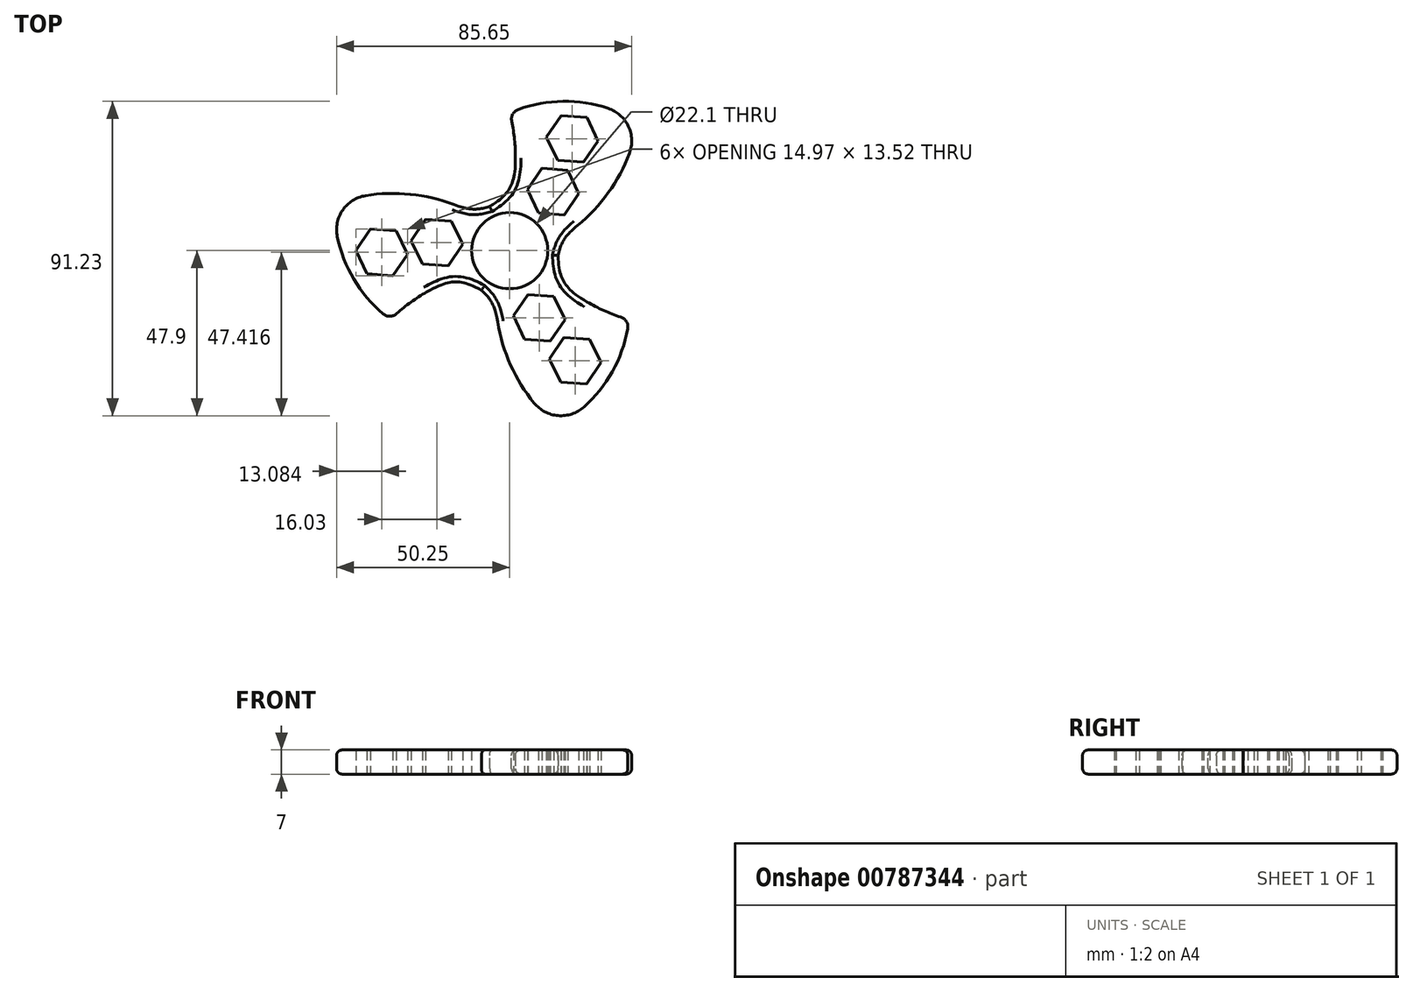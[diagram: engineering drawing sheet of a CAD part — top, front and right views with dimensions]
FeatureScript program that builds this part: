
annotation { "Feature Type Name" : "Feature", "Feature Type Description" : "" }
export const myFeature = defineFeature(function(context is Context, id is Id, definition is map)
    precondition{}
    {
        {
            var Q0;
            Q0=qCreatedBy(makeId("Top.planeOp"),FACE);
            var sketch = newSketch(context, id + "F0", { "sketchPlane" : qUnion([Q0])});
            skCircle(sketch, "E0", {"center": v(0, 0) * mm, "radius": 14 * mm});
            skArc(sketch, "E1", {"start": v(0, 14) * mm, "mid": v(1.66, 27) * mm, "end": v(0, 40) * mm});
            skPoint(sketch, "E2", {"position": v(0, 40) * mm});
            skLineSegment(sketch, "E3", {"start": v(0, 0) * mm, "end": v(37.22, 37.22) * mm, "construction": true});
            skPoint(sketch, "E4", {"position": v(37.22, 37.22) * mm});
            skArc(sketch, "E5.trimOffspring", {"start": v(37.22, 37.22) * mm, "mid": v(18.96, 43.22) * mm, "end": v(0, 40) * mm});
            skArc(sketch, "E6.trimOffspring", {"start": v(13.66, 3.08) * mm, "mid": v(29.15, 17.6) * mm, "end": v(37.22, 37.22) * mm});
            skCircle(sketch, "E7", {"center": v(0, 0) * mm, "radius": 11.05 * mm});
            skCircle(sketch, "E8.cCircle", {"center": v(18.16, 32.43) * mm, "radius": 6.5 * mm, "construction": true});
            skLineSegment(sketch, "E8.0", {"start": v(25.65, 31.87) * mm, "end": v(21.42, 25.67) * mm});
            skLineSegment(sketch, "E8.1", {"start": v(21.42, 25.67) * mm, "end": v(13.94, 26.23) * mm});
            skLineSegment(sketch, "E8.2", {"start": v(13.94, 26.23) * mm, "end": v(10.68, 32.99) * mm});
            skLineSegment(sketch, "E8.3", {"start": v(10.68, 32.99) * mm, "end": v(14.9, 39.19) * mm});
            skLineSegment(sketch, "E8.4", {"start": v(14.9, 39.19) * mm, "end": v(22.39, 38.63) * mm});
            skLineSegment(sketch, "E8.5", {"start": v(22.39, 38.63) * mm, "end": v(25.65, 31.87) * mm});
            skPoint(sketch, "E8.0.midPoint", {"position": v(23.54, 28.77) * mm});
            skLineSegment(sketch, "E9", {"start": v(18.65, 38.91) * mm, "end": v(18.16, 32.43) * mm, "construction": true});
            skLineSegment(sketch, "E10", {"start": v(0, 14) * mm, "end": v(13.66, 3.08) * mm, "construction": true});
            skLineSegment(sketch, "E11", {"start": v(6.83, 8.54) * mm, "end": v(20.57, 25.73) * mm, "construction": true});
            skLineSegment(sketch, "E12", {"start": v(37.22, 37.22) * mm, "end": v(0, 40) * mm, "construction": true});
            skCircle(sketch, "E13.cCircle", {"center": v(12.6, 17.14) * mm, "radius": 6.5 * mm, "construction": true});
            skLineSegment(sketch, "E13.0", {"start": v(9.33, 23.9) * mm, "end": v(16.82, 23.34) * mm});
            skLineSegment(sketch, "E13.1", {"start": v(16.82, 23.34) * mm, "end": v(20.08, 16.58) * mm});
            skLineSegment(sketch, "E13.2", {"start": v(20.08, 16.58) * mm, "end": v(15.85, 10.38) * mm});
            skLineSegment(sketch, "E13.3", {"start": v(15.85, 10.38) * mm, "end": v(8.36, 10.93) * mm});
            skLineSegment(sketch, "E13.4", {"start": v(8.36, 10.93) * mm, "end": v(5.1, 17.7) * mm});
            skLineSegment(sketch, "E13.5", {"start": v(5.1, 17.7) * mm, "end": v(9.33, 23.9) * mm});
            skPoint(sketch, "E13.0.midPoint", {"position": v(13.07, 23.62) * mm});
            skPoint(sketch, "E14.1.18", {"position": v(-1.49, 0.86) * mm});
            skPoint(sketch, "E14.1.24", {"position": v(-1.49, 0.86) * mm});
            skPoint(sketch, "E14.2.18", {"position": v(-1.49, -0.86) * mm});
            skPoint(sketch, "E14.2.24", {"position": v(-1.49, -0.86) * mm});
            skPoint(sketch, "E14.center", {"position": v(-1, 0) * mm});
            skPoint(sketch, "E15", {"position": v(13.7, 17.14) * mm});
            skCircle(sketch, "E16.1.0", {"center": v(-21.14, 2.34) * mm, "radius": 6.5 * mm, "construction": true});
            skLineSegment(sketch, "E16.1.1", {"start": v(-33.9, -7.24) * mm, "end": v(-41.4, -6.69) * mm});
            skPoint(sketch, "E16.1.2", {"position": v(1.49, -0.86) * mm});
            skLineSegment(sketch, "E16.1.3", {"start": v(-10.81, 1.64) * mm, "end": v(-32.57, 4.95) * mm, "construction": true});
            skArc(sketch, "E16.1.4", {"start": v(-50.85, 13.62) * mm, "mid": v(-46.9, -5.2) * mm, "end": v(-34.64, -20) * mm});
            skLineSegment(sketch, "E16.1.5", {"start": v(-24.4, 9.1) * mm, "end": v(-16.91, 8.54) * mm});
            skLineSegment(sketch, "E16.1.6", {"start": v(-50.85, 13.62) * mm, "end": v(-34.64, -20) * mm, "construction": true});
            skLineSegment(sketch, "E16.1.8", {"start": v(-28.62, 2.9) * mm, "end": v(-24.4, 9.1) * mm});
            skArc(sketch, "E16.1.9", {"start": v(-12.12, -7) * mm, "mid": v(-24.21, -12.06) * mm, "end": v(-34.64, -20) * mm});
            skLineSegment(sketch, "E16.1.10", {"start": v(-44.65, 0.07) * mm, "end": v(-40.42, 6.28) * mm});
            skPoint(sketch, "E16.1.11", {"position": v(-21.69, 3.3) * mm});
            skLineSegment(sketch, "E16.1.12", {"start": v(-17.88, -4.43) * mm, "end": v(-25.36, -3.87) * mm});
            skCircle(sketch, "E16.1.13", {"center": v(-37.17, -0.48) * mm, "radius": 6.5 * mm, "construction": true});
            skArc(sketch, "E16.1.14", {"start": v(-9.5, 10.28) * mm, "mid": v(-29.81, 16.45) * mm, "end": v(-50.85, 13.62) * mm});
            skPoint(sketch, "E16.1.15", {"position": v(-50.85, 13.62) * mm});
            skLineSegment(sketch, "E16.1.16", {"start": v(-29.68, -1.04) * mm, "end": v(-33.9, -7.24) * mm});
            skPoint(sketch, "E16.1.17", {"position": v(-36.68, 6) * mm});
            skLineSegment(sketch, "E16.1.18", {"start": v(-16.91, 8.54) * mm, "end": v(-13.65, 1.78) * mm});
            skLineSegment(sketch, "E16.1.19", {"start": v(-12.12, -7) * mm, "end": v(-9.5, 10.28) * mm, "construction": true});
            skLineSegment(sketch, "E16.1.20", {"start": v(-43.02, -3.3) * mm, "end": v(-37.17, -0.48) * mm, "construction": true});
            skPoint(sketch, "E16.1.21", {"position": v(-34.64, -20) * mm});
            skPoint(sketch, "E16.1.22", {"position": v(0.5, -0.86) * mm});
            skPoint(sketch, "E16.1.23", {"position": v(-27, -0.49) * mm});
            skPoint(sketch, "E16.1.24", {"position": v(1.49, -0.86) * mm});
            skLineSegment(sketch, "E16.1.25", {"start": v(-40.42, 6.28) * mm, "end": v(-32.94, 5.72) * mm});
            skLineSegment(sketch, "E16.1.26", {"start": v(-32.94, 5.72) * mm, "end": v(-29.68, -1.04) * mm});
            skLineSegment(sketch, "E16.1.27", {"start": v(-41.4, -6.69) * mm, "end": v(-44.65, 0.07) * mm});
            skLineSegment(sketch, "E16.1.29", {"start": v(-25.36, -3.87) * mm, "end": v(-28.62, 2.9) * mm});
            skLineSegment(sketch, "E16.1.30", {"start": v(-13.65, 1.78) * mm, "end": v(-17.88, -4.43) * mm});
            skCircle(sketch, "E16.2.0", {"center": v(8.55, -19.47) * mm, "radius": 6.5 * mm, "construction": true});
            skLineSegment(sketch, "E16.2.1", {"start": v(23.23, -25.74) * mm, "end": v(26.49, -32.5) * mm});
            skPoint(sketch, "E16.2.2", {"position": v(0, 1.72) * mm});
            skLineSegment(sketch, "E16.2.3", {"start": v(3.98, -10.18) * mm, "end": v(12, -30.68) * mm, "construction": true});
            skArc(sketch, "E16.2.4", {"start": v(13.62, -50.85) * mm, "mid": v(27.95, -38.03) * mm, "end": v(34.64, -20) * mm});
            skLineSegment(sketch, "E16.2.5", {"start": v(4.32, -25.68) * mm, "end": v(1.06, -18.91) * mm});
            skLineSegment(sketch, "E16.2.6", {"start": v(13.62, -50.85) * mm, "end": v(34.64, -20) * mm, "construction": true});
            skLineSegment(sketch, "E16.2.8", {"start": v(11.8, -26.23) * mm, "end": v(4.32, -25.68) * mm});
            skArc(sketch, "E16.2.9", {"start": v(12.12, -7) * mm, "mid": v(22.55, -14.94) * mm, "end": v(34.64, -20) * mm});
            skLineSegment(sketch, "E16.2.10", {"start": v(22.26, -38.7) * mm, "end": v(14.78, -38.15) * mm});
            skPoint(sketch, "E16.2.11", {"position": v(8, -20.43) * mm});
            skLineSegment(sketch, "E16.2.12", {"start": v(12.77, -13.27) * mm, "end": v(16.03, -20.03) * mm});
            skCircle(sketch, "E16.2.13", {"center": v(19, -31.94) * mm, "radius": 6.5 * mm, "construction": true});
            skArc(sketch, "E16.2.14", {"start": v(-4.16, -13.37) * mm, "mid": v(0.66, -34.04) * mm, "end": v(13.62, -50.85) * mm});
            skPoint(sketch, "E16.2.15", {"position": v(13.62, -50.85) * mm});
            skLineSegment(sketch, "E16.2.16", {"start": v(15.74, -25.18) * mm, "end": v(23.23, -25.74) * mm});
            skPoint(sketch, "E16.2.17", {"position": v(13.15, -34.77) * mm});
            skLineSegment(sketch, "E16.2.18", {"start": v(1.06, -18.91) * mm, "end": v(5.29, -12.71) * mm});
            skLineSegment(sketch, "E16.2.19", {"start": v(12.12, -7) * mm, "end": v(-4.16, -13.37) * mm, "construction": true});
            skLineSegment(sketch, "E16.2.20", {"start": v(24.37, -35.6) * mm, "end": v(19, -31.94) * mm, "construction": true});
            skPoint(sketch, "E16.2.21", {"position": v(34.64, -20) * mm});
            skPoint(sketch, "E16.2.22", {"position": v(0.5, 0.86) * mm});
            skPoint(sketch, "E16.2.23", {"position": v(13.92, -23.13) * mm});
            skPoint(sketch, "E16.2.24", {"position": v(0, 1.72) * mm});
            skLineSegment(sketch, "E16.2.25", {"start": v(14.78, -38.15) * mm, "end": v(11.52, -31.39) * mm});
            skLineSegment(sketch, "E16.2.26", {"start": v(11.52, -31.39) * mm, "end": v(15.74, -25.18) * mm});
            skLineSegment(sketch, "E16.2.27", {"start": v(26.49, -32.5) * mm, "end": v(22.26, -38.7) * mm});
            skLineSegment(sketch, "E16.2.29", {"start": v(16.03, -20.03) * mm, "end": v(11.8, -26.23) * mm});
            skLineSegment(sketch, "E16.2.30", {"start": v(5.29, -12.71) * mm, "end": v(12.77, -13.27) * mm});
            skSolve(sketch);
        }
        {
            var Q0;
            Q0 = qSketchRegion(id + "F0", true);
            extrude(context, id + "F1", {"entities" : qUnion([Q0]), "depth" : 7 * mm, "offsetDistance" : 25 * mm});
        }
        {
            var Q0;
            Q0=makeQuery(id+"F1.opExtrude","SWEPT_EDGE",EDGE,{"disambiguationData":[OSD([sQuery(id+"F0.wireOp",EDGE,"E16.1.4"),sQuery(id+"F0.wireOp",EDGE,"E16.1.14")])]});
            var Q1;
            Q1=makeQuery(id+"F1.opExtrude","SWEPT_EDGE",EDGE,{"disambiguationData":[OSD([sQuery(id+"F0.wireOp",EDGE,"E5.trimOffspring"),sQuery(id+"F0.wireOp",EDGE,"E6.trimOffspring")])]});
            var Q2;
            Q2=makeQuery(id+"F1.opExtrude","SWEPT_EDGE",EDGE,{"disambiguationData":[OSD([sQuery(id+"F0.wireOp",EDGE,"E16.2.4"),sQuery(id+"F0.wireOp",EDGE,"E16.2.14")])]});
            fillet(context, id + "F2", {"entities" : qUnion([Q0, Q1, Q2]), "radius" : 10 * mm, "tangentPropagation" : true, "allowEdgeOverflow" : false});
        }
        {
            var Q0;
            Q0=makeQuery(id+"F1.opExtrude","SWEPT_EDGE",EDGE,{"disambiguationData":[OSD([sQuery(id+"F0.wireOp",EDGE,"E1"),sQuery(id+"F0.wireOp",EDGE,"E5.trimOffspring")])]});
            var Q1;
            Q1=makeQuery(id+"F1.opExtrude","SWEPT_EDGE",EDGE,{"disambiguationData":[OSD([sQuery(id+"F0.wireOp",EDGE,"E16.1.4"),sQuery(id+"F0.wireOp",EDGE,"E16.1.9")])]});
            var Q2;
            Q2=makeQuery(id+"F1.opExtrude","SWEPT_EDGE",EDGE,{"disambiguationData":[OSD([sQuery(id+"F0.wireOp",EDGE,"E16.2.4"),sQuery(id+"F0.wireOp",EDGE,"E16.2.9")])]});
            fillet(context, id + "F3", {"entities" : qUnion([Q0, Q1, Q2]), "radius" : 3 * mm, "tangentPropagation" : true, "allowEdgeOverflow" : false});
        }
        {
            var Q0;
            Q0=makeQuery(id+"F1.opExtrude","SWEPT_EDGE",EDGE,{"disambiguationData":[OSD([sQuery(id+"F0.wireOp",EDGE,"E0"),sQuery(id+"F0.wireOp",EDGE,"544d86c7-8deb-4338-a2d6-1758b23e3787.2.16")])]});
            var Q1;
            Q1=makeQuery(id+"F1.opExtrude","SWEPT_EDGE",EDGE,{"disambiguationData":[OSD([sQuery(id+"F0.wireOp",EDGE,"E0"),sQuery(id+"F0.wireOp",EDGE,"E6.trimOffspring")])]});
            var Q2;
            Q2=makeQuery(id+"F1.opExtrude","SWEPT_EDGE",EDGE,{"disambiguationData":[OSD([sQuery(id+"F0.wireOp",EDGE,"E0"),sQuery(id+"F0.wireOp",EDGE,"E1")])]});
            var Q3;
            Q3=makeQuery(id+"F1.opExtrude","SWEPT_EDGE",EDGE,{"disambiguationData":[OSD([sQuery(id+"F0.wireOp",EDGE,"E0"),sQuery(id+"F0.wireOp",EDGE,"544d86c7-8deb-4338-a2d6-1758b23e3787.1.5")])]});
            var Q4;
            Q4=makeQuery(id+"F1.opExtrude","SWEPT_EDGE",EDGE,{"disambiguationData":[OSD([sQuery(id+"F0.wireOp",EDGE,"E0"),sQuery(id+"F0.wireOp",EDGE,"544d86c7-8deb-4338-a2d6-1758b23e3787.1.16")])]});
            var Q5;
            Q5=makeQuery(id+"F1.opExtrude","SWEPT_EDGE",EDGE,{"disambiguationData":[OSD([sQuery(id+"F0.wireOp",EDGE,"E0"),sQuery(id+"F0.wireOp",EDGE,"544d86c7-8deb-4338-a2d6-1758b23e3787.2.5")])]});
            fillet(context, id + "F4", {"entities" : qUnion([Q0, Q1, Q2, Q3, Q4, Q5]), "radius" : 17 * mm, "rho" : .6, "crossSection" : FilletCrossSection.CONIC, "allowEdgeOverflow" : false});
        }
        {
            var Q0;
            {var subQ0=sQuery(id+"F0.wireOp",EDGE,"E6.trimOffspring");var subQ1=sQuery(id+"F0.wireOp",EDGE,"E5.trimOffspring");Q0=makeQuery(id+"F2.opFillet","BLEND_EDGE",EDGE,{"blendedFrom":[makeQuery(id+"F1.opExtrude","SWEPT_EDGE",EDGE,{"disambiguationData":[OSD([subQ1,subQ0])]}),makeQuery(id+"F1.opExtrude","CAP_FACE",FACE,{"disambiguationData":[OSD([sQuery(id+"F0.wireOp",EDGE,"E0"),sQuery(id+"F0.wireOp",EDGE,"E1"),subQ1,subQ0,sQuery(id+"F0.wireOp",EDGE,"E7"),sQuery(id+"F0.wireOp",EDGE,"E8.0"),sQuery(id+"F0.wireOp",EDGE,"E8.1"),sQuery(id+"F0.wireOp",EDGE,"E8.2"),sQuery(id+"F0.wireOp",EDGE,"E8.3"),sQuery(id+"F0.wireOp",EDGE,"E8.4"),sQuery(id+"F0.wireOp",EDGE,"E8.5"),sQuery(id+"F0.wireOp",EDGE,"E13.0"),sQuery(id+"F0.wireOp",EDGE,"E13.1"),sQuery(id+"F0.wireOp",EDGE,"E13.2"),sQuery(id+"F0.wireOp",EDGE,"E13.3"),sQuery(id+"F0.wireOp",EDGE,"E13.4"),sQuery(id+"F0.wireOp",EDGE,"E13.5"),sQuery(id+"F0.wireOp",EDGE,"E16.1.1"),sQuery(id+"F0.wireOp",EDGE,"E16.1.4"),sQuery(id+"F0.wireOp",EDGE,"E16.1.5"),sQuery(id+"F0.wireOp",EDGE,"E16.1.8"),sQuery(id+"F0.wireOp",EDGE,"E16.1.9"),sQuery(id+"F0.wireOp",EDGE,"E16.1.10"),sQuery(id+"F0.wireOp",EDGE,"E16.1.12"),sQuery(id+"F0.wireOp",EDGE,"E16.1.14"),sQuery(id+"F0.wireOp",EDGE,"E16.1.16"),sQuery(id+"F0.wireOp",EDGE,"E16.1.18"),sQuery(id+"F0.wireOp",EDGE,"E16.1.25"),sQuery(id+"F0.wireOp",EDGE,"E16.1.26"),sQuery(id+"F0.wireOp",EDGE,"E16.1.27"),sQuery(id+"F0.wireOp",EDGE,"E16.1.29"),sQuery(id+"F0.wireOp",EDGE,"E16.1.30"),sQuery(id+"F0.wireOp",EDGE,"E16.2.1"),sQuery(id+"F0.wireOp",EDGE,"E16.2.4"),sQuery(id+"F0.wireOp",EDGE,"E16.2.5"),sQuery(id+"F0.wireOp",EDGE,"E16.2.8"),sQuery(id+"F0.wireOp",EDGE,"E16.2.9"),sQuery(id+"F0.wireOp",EDGE,"E16.2.10"),sQuery(id+"F0.wireOp",EDGE,"E16.2.12"),sQuery(id+"F0.wireOp",EDGE,"E16.2.14"),sQuery(id+"F0.wireOp",EDGE,"E16.2.16"),sQuery(id+"F0.wireOp",EDGE,"E16.2.18"),sQuery(id+"F0.wireOp",EDGE,"E16.2.25"),sQuery(id+"F0.wireOp",EDGE,"E16.2.26"),sQuery(id+"F0.wireOp",EDGE,"E16.2.27"),sQuery(id+"F0.wireOp",EDGE,"E16.2.29"),sQuery(id+"F0.wireOp",EDGE,"E16.2.30")])],"isStart":false})],"blendedInto":[makeQuery(id+"F1.opExtrude","CAP_FACE",FACE,{"disambiguationData":[OSD([sQuery(id+"F0.wireOp",EDGE,"E0"),sQuery(id+"F0.wireOp",EDGE,"E1"),subQ1,subQ0,sQuery(id+"F0.wireOp",EDGE,"E7"),sQuery(id+"F0.wireOp",EDGE,"E8.0"),sQuery(id+"F0.wireOp",EDGE,"E8.1"),sQuery(id+"F0.wireOp",EDGE,"E8.2"),sQuery(id+"F0.wireOp",EDGE,"E8.3"),sQuery(id+"F0.wireOp",EDGE,"E8.4"),sQuery(id+"F0.wireOp",EDGE,"E8.5"),sQuery(id+"F0.wireOp",EDGE,"E13.0"),sQuery(id+"F0.wireOp",EDGE,"E13.1"),sQuery(id+"F0.wireOp",EDGE,"E13.2"),sQuery(id+"F0.wireOp",EDGE,"E13.3"),sQuery(id+"F0.wireOp",EDGE,"E13.4"),sQuery(id+"F0.wireOp",EDGE,"E13.5"),sQuery(id+"F0.wireOp",EDGE,"E16.1.1"),sQuery(id+"F0.wireOp",EDGE,"E16.1.4"),sQuery(id+"F0.wireOp",EDGE,"E16.1.5"),sQuery(id+"F0.wireOp",EDGE,"E16.1.8"),sQuery(id+"F0.wireOp",EDGE,"E16.1.9"),sQuery(id+"F0.wireOp",EDGE,"E16.1.10"),sQuery(id+"F0.wireOp",EDGE,"E16.1.12"),sQuery(id+"F0.wireOp",EDGE,"E16.1.14"),sQuery(id+"F0.wireOp",EDGE,"E16.1.16"),sQuery(id+"F0.wireOp",EDGE,"E16.1.18"),sQuery(id+"F0.wireOp",EDGE,"E16.1.25"),sQuery(id+"F0.wireOp",EDGE,"E16.1.26"),sQuery(id+"F0.wireOp",EDGE,"E16.1.27"),sQuery(id+"F0.wireOp",EDGE,"E16.1.29"),sQuery(id+"F0.wireOp",EDGE,"E16.1.30"),sQuery(id+"F0.wireOp",EDGE,"E16.2.1"),sQuery(id+"F0.wireOp",EDGE,"E16.2.4"),sQuery(id+"F0.wireOp",EDGE,"E16.2.5"),sQuery(id+"F0.wireOp",EDGE,"E16.2.8"),sQuery(id+"F0.wireOp",EDGE,"E16.2.9"),sQuery(id+"F0.wireOp",EDGE,"E16.2.10"),sQuery(id+"F0.wireOp",EDGE,"E16.2.12"),sQuery(id+"F0.wireOp",EDGE,"E16.2.14"),sQuery(id+"F0.wireOp",EDGE,"E16.2.16"),sQuery(id+"F0.wireOp",EDGE,"E16.2.18"),sQuery(id+"F0.wireOp",EDGE,"E16.2.25"),sQuery(id+"F0.wireOp",EDGE,"E16.2.26"),sQuery(id+"F0.wireOp",EDGE,"E16.2.27"),sQuery(id+"F0.wireOp",EDGE,"E16.2.29"),sQuery(id+"F0.wireOp",EDGE,"E16.2.30")])],"isStart":false})]});}
            var Q1;
            {var subQ0=sQuery(id+"F0.wireOp",EDGE,"E6.trimOffspring");var subQ1=sQuery(id+"F0.wireOp",EDGE,"E5.trimOffspring");Q1=makeQuery(id+"F2.opFillet","BLEND_EDGE",EDGE,{"blendedFrom":[makeQuery(id+"F1.opExtrude","SWEPT_EDGE",EDGE,{"disambiguationData":[OSD([subQ1,subQ0])]}),makeQuery(id+"F1.opExtrude","CAP_FACE",FACE,{"disambiguationData":[OSD([sQuery(id+"F0.wireOp",EDGE,"E0"),sQuery(id+"F0.wireOp",EDGE,"E1"),subQ1,subQ0,sQuery(id+"F0.wireOp",EDGE,"E7"),sQuery(id+"F0.wireOp",EDGE,"E8.0"),sQuery(id+"F0.wireOp",EDGE,"E8.1"),sQuery(id+"F0.wireOp",EDGE,"E8.2"),sQuery(id+"F0.wireOp",EDGE,"E8.3"),sQuery(id+"F0.wireOp",EDGE,"E8.4"),sQuery(id+"F0.wireOp",EDGE,"E8.5"),sQuery(id+"F0.wireOp",EDGE,"E13.0"),sQuery(id+"F0.wireOp",EDGE,"E13.1"),sQuery(id+"F0.wireOp",EDGE,"E13.2"),sQuery(id+"F0.wireOp",EDGE,"E13.3"),sQuery(id+"F0.wireOp",EDGE,"E13.4"),sQuery(id+"F0.wireOp",EDGE,"E13.5"),sQuery(id+"F0.wireOp",EDGE,"E16.1.1"),sQuery(id+"F0.wireOp",EDGE,"E16.1.4"),sQuery(id+"F0.wireOp",EDGE,"E16.1.5"),sQuery(id+"F0.wireOp",EDGE,"E16.1.8"),sQuery(id+"F0.wireOp",EDGE,"E16.1.9"),sQuery(id+"F0.wireOp",EDGE,"E16.1.10"),sQuery(id+"F0.wireOp",EDGE,"E16.1.12"),sQuery(id+"F0.wireOp",EDGE,"E16.1.14"),sQuery(id+"F0.wireOp",EDGE,"E16.1.16"),sQuery(id+"F0.wireOp",EDGE,"E16.1.18"),sQuery(id+"F0.wireOp",EDGE,"E16.1.25"),sQuery(id+"F0.wireOp",EDGE,"E16.1.26"),sQuery(id+"F0.wireOp",EDGE,"E16.1.27"),sQuery(id+"F0.wireOp",EDGE,"E16.1.29"),sQuery(id+"F0.wireOp",EDGE,"E16.1.30"),sQuery(id+"F0.wireOp",EDGE,"E16.2.1"),sQuery(id+"F0.wireOp",EDGE,"E16.2.4"),sQuery(id+"F0.wireOp",EDGE,"E16.2.5"),sQuery(id+"F0.wireOp",EDGE,"E16.2.8"),sQuery(id+"F0.wireOp",EDGE,"E16.2.9"),sQuery(id+"F0.wireOp",EDGE,"E16.2.10"),sQuery(id+"F0.wireOp",EDGE,"E16.2.12"),sQuery(id+"F0.wireOp",EDGE,"E16.2.14"),sQuery(id+"F0.wireOp",EDGE,"E16.2.16"),sQuery(id+"F0.wireOp",EDGE,"E16.2.18"),sQuery(id+"F0.wireOp",EDGE,"E16.2.25"),sQuery(id+"F0.wireOp",EDGE,"E16.2.26"),sQuery(id+"F0.wireOp",EDGE,"E16.2.27"),sQuery(id+"F0.wireOp",EDGE,"E16.2.29"),sQuery(id+"F0.wireOp",EDGE,"E16.2.30")])],"isStart":true})],"blendedInto":[makeQuery(id+"F1.opExtrude","CAP_FACE",FACE,{"disambiguationData":[OSD([sQuery(id+"F0.wireOp",EDGE,"E0"),sQuery(id+"F0.wireOp",EDGE,"E1"),subQ1,subQ0,sQuery(id+"F0.wireOp",EDGE,"E7"),sQuery(id+"F0.wireOp",EDGE,"E8.0"),sQuery(id+"F0.wireOp",EDGE,"E8.1"),sQuery(id+"F0.wireOp",EDGE,"E8.2"),sQuery(id+"F0.wireOp",EDGE,"E8.3"),sQuery(id+"F0.wireOp",EDGE,"E8.4"),sQuery(id+"F0.wireOp",EDGE,"E8.5"),sQuery(id+"F0.wireOp",EDGE,"E13.0"),sQuery(id+"F0.wireOp",EDGE,"E13.1"),sQuery(id+"F0.wireOp",EDGE,"E13.2"),sQuery(id+"F0.wireOp",EDGE,"E13.3"),sQuery(id+"F0.wireOp",EDGE,"E13.4"),sQuery(id+"F0.wireOp",EDGE,"E13.5"),sQuery(id+"F0.wireOp",EDGE,"E16.1.1"),sQuery(id+"F0.wireOp",EDGE,"E16.1.4"),sQuery(id+"F0.wireOp",EDGE,"E16.1.5"),sQuery(id+"F0.wireOp",EDGE,"E16.1.8"),sQuery(id+"F0.wireOp",EDGE,"E16.1.9"),sQuery(id+"F0.wireOp",EDGE,"E16.1.10"),sQuery(id+"F0.wireOp",EDGE,"E16.1.12"),sQuery(id+"F0.wireOp",EDGE,"E16.1.14"),sQuery(id+"F0.wireOp",EDGE,"E16.1.16"),sQuery(id+"F0.wireOp",EDGE,"E16.1.18"),sQuery(id+"F0.wireOp",EDGE,"E16.1.25"),sQuery(id+"F0.wireOp",EDGE,"E16.1.26"),sQuery(id+"F0.wireOp",EDGE,"E16.1.27"),sQuery(id+"F0.wireOp",EDGE,"E16.1.29"),sQuery(id+"F0.wireOp",EDGE,"E16.1.30"),sQuery(id+"F0.wireOp",EDGE,"E16.2.1"),sQuery(id+"F0.wireOp",EDGE,"E16.2.4"),sQuery(id+"F0.wireOp",EDGE,"E16.2.5"),sQuery(id+"F0.wireOp",EDGE,"E16.2.8"),sQuery(id+"F0.wireOp",EDGE,"E16.2.9"),sQuery(id+"F0.wireOp",EDGE,"E16.2.10"),sQuery(id+"F0.wireOp",EDGE,"E16.2.12"),sQuery(id+"F0.wireOp",EDGE,"E16.2.14"),sQuery(id+"F0.wireOp",EDGE,"E16.2.16"),sQuery(id+"F0.wireOp",EDGE,"E16.2.18"),sQuery(id+"F0.wireOp",EDGE,"E16.2.25"),sQuery(id+"F0.wireOp",EDGE,"E16.2.26"),sQuery(id+"F0.wireOp",EDGE,"E16.2.27"),sQuery(id+"F0.wireOp",EDGE,"E16.2.29"),sQuery(id+"F0.wireOp",EDGE,"E16.2.30")])],"isStart":true})]});}
            var Q2;
            {var subQ0=sQuery(id+"F0.wireOp",EDGE,"E16.1.14");var subQ1=sQuery(id+"F0.wireOp",EDGE,"E16.1.4");Q2=makeQuery(id+"F2.opFillet","BLEND_EDGE",EDGE,{"blendedFrom":[makeQuery(id+"F1.opExtrude","SWEPT_EDGE",EDGE,{"disambiguationData":[OSD([subQ1,subQ0])]}),makeQuery(id+"F1.opExtrude","CAP_FACE",FACE,{"disambiguationData":[OSD([sQuery(id+"F0.wireOp",EDGE,"E0"),sQuery(id+"F0.wireOp",EDGE,"E1"),sQuery(id+"F0.wireOp",EDGE,"E5.trimOffspring"),sQuery(id+"F0.wireOp",EDGE,"E6.trimOffspring"),sQuery(id+"F0.wireOp",EDGE,"E7"),sQuery(id+"F0.wireOp",EDGE,"E8.0"),sQuery(id+"F0.wireOp",EDGE,"E8.1"),sQuery(id+"F0.wireOp",EDGE,"E8.2"),sQuery(id+"F0.wireOp",EDGE,"E8.3"),sQuery(id+"F0.wireOp",EDGE,"E8.4"),sQuery(id+"F0.wireOp",EDGE,"E8.5"),sQuery(id+"F0.wireOp",EDGE,"E13.0"),sQuery(id+"F0.wireOp",EDGE,"E13.1"),sQuery(id+"F0.wireOp",EDGE,"E13.2"),sQuery(id+"F0.wireOp",EDGE,"E13.3"),sQuery(id+"F0.wireOp",EDGE,"E13.4"),sQuery(id+"F0.wireOp",EDGE,"E13.5"),sQuery(id+"F0.wireOp",EDGE,"E16.1.1"),subQ1,sQuery(id+"F0.wireOp",EDGE,"E16.1.5"),sQuery(id+"F0.wireOp",EDGE,"E16.1.8"),sQuery(id+"F0.wireOp",EDGE,"E16.1.9"),sQuery(id+"F0.wireOp",EDGE,"E16.1.10"),sQuery(id+"F0.wireOp",EDGE,"E16.1.12"),subQ0,sQuery(id+"F0.wireOp",EDGE,"E16.1.16"),sQuery(id+"F0.wireOp",EDGE,"E16.1.18"),sQuery(id+"F0.wireOp",EDGE,"E16.1.25"),sQuery(id+"F0.wireOp",EDGE,"E16.1.26"),sQuery(id+"F0.wireOp",EDGE,"E16.1.27"),sQuery(id+"F0.wireOp",EDGE,"E16.1.29"),sQuery(id+"F0.wireOp",EDGE,"E16.1.30"),sQuery(id+"F0.wireOp",EDGE,"E16.2.1"),sQuery(id+"F0.wireOp",EDGE,"E16.2.4"),sQuery(id+"F0.wireOp",EDGE,"E16.2.5"),sQuery(id+"F0.wireOp",EDGE,"E16.2.8"),sQuery(id+"F0.wireOp",EDGE,"E16.2.9"),sQuery(id+"F0.wireOp",EDGE,"E16.2.10"),sQuery(id+"F0.wireOp",EDGE,"E16.2.12"),sQuery(id+"F0.wireOp",EDGE,"E16.2.14"),sQuery(id+"F0.wireOp",EDGE,"E16.2.16"),sQuery(id+"F0.wireOp",EDGE,"E16.2.18"),sQuery(id+"F0.wireOp",EDGE,"E16.2.25"),sQuery(id+"F0.wireOp",EDGE,"E16.2.26"),sQuery(id+"F0.wireOp",EDGE,"E16.2.27"),sQuery(id+"F0.wireOp",EDGE,"E16.2.29"),sQuery(id+"F0.wireOp",EDGE,"E16.2.30")])],"isStart":false})],"blendedInto":[makeQuery(id+"F1.opExtrude","CAP_FACE",FACE,{"disambiguationData":[OSD([sQuery(id+"F0.wireOp",EDGE,"E0"),sQuery(id+"F0.wireOp",EDGE,"E1"),sQuery(id+"F0.wireOp",EDGE,"E5.trimOffspring"),sQuery(id+"F0.wireOp",EDGE,"E6.trimOffspring"),sQuery(id+"F0.wireOp",EDGE,"E7"),sQuery(id+"F0.wireOp",EDGE,"E8.0"),sQuery(id+"F0.wireOp",EDGE,"E8.1"),sQuery(id+"F0.wireOp",EDGE,"E8.2"),sQuery(id+"F0.wireOp",EDGE,"E8.3"),sQuery(id+"F0.wireOp",EDGE,"E8.4"),sQuery(id+"F0.wireOp",EDGE,"E8.5"),sQuery(id+"F0.wireOp",EDGE,"E13.0"),sQuery(id+"F0.wireOp",EDGE,"E13.1"),sQuery(id+"F0.wireOp",EDGE,"E13.2"),sQuery(id+"F0.wireOp",EDGE,"E13.3"),sQuery(id+"F0.wireOp",EDGE,"E13.4"),sQuery(id+"F0.wireOp",EDGE,"E13.5"),sQuery(id+"F0.wireOp",EDGE,"E16.1.1"),subQ1,sQuery(id+"F0.wireOp",EDGE,"E16.1.5"),sQuery(id+"F0.wireOp",EDGE,"E16.1.8"),sQuery(id+"F0.wireOp",EDGE,"E16.1.9"),sQuery(id+"F0.wireOp",EDGE,"E16.1.10"),sQuery(id+"F0.wireOp",EDGE,"E16.1.12"),subQ0,sQuery(id+"F0.wireOp",EDGE,"E16.1.16"),sQuery(id+"F0.wireOp",EDGE,"E16.1.18"),sQuery(id+"F0.wireOp",EDGE,"E16.1.25"),sQuery(id+"F0.wireOp",EDGE,"E16.1.26"),sQuery(id+"F0.wireOp",EDGE,"E16.1.27"),sQuery(id+"F0.wireOp",EDGE,"E16.1.29"),sQuery(id+"F0.wireOp",EDGE,"E16.1.30"),sQuery(id+"F0.wireOp",EDGE,"E16.2.1"),sQuery(id+"F0.wireOp",EDGE,"E16.2.4"),sQuery(id+"F0.wireOp",EDGE,"E16.2.5"),sQuery(id+"F0.wireOp",EDGE,"E16.2.8"),sQuery(id+"F0.wireOp",EDGE,"E16.2.9"),sQuery(id+"F0.wireOp",EDGE,"E16.2.10"),sQuery(id+"F0.wireOp",EDGE,"E16.2.12"),sQuery(id+"F0.wireOp",EDGE,"E16.2.14"),sQuery(id+"F0.wireOp",EDGE,"E16.2.16"),sQuery(id+"F0.wireOp",EDGE,"E16.2.18"),sQuery(id+"F0.wireOp",EDGE,"E16.2.25"),sQuery(id+"F0.wireOp",EDGE,"E16.2.26"),sQuery(id+"F0.wireOp",EDGE,"E16.2.27"),sQuery(id+"F0.wireOp",EDGE,"E16.2.29"),sQuery(id+"F0.wireOp",EDGE,"E16.2.30")])],"isStart":false})]});}
            var Q3;
            {var subQ0=sQuery(id+"F0.wireOp",EDGE,"E16.1.14");var subQ1=sQuery(id+"F0.wireOp",EDGE,"E16.1.4");Q3=makeQuery(id+"F2.opFillet","BLEND_EDGE",EDGE,{"blendedFrom":[makeQuery(id+"F1.opExtrude","SWEPT_EDGE",EDGE,{"disambiguationData":[OSD([subQ1,subQ0])]}),makeQuery(id+"F1.opExtrude","CAP_FACE",FACE,{"disambiguationData":[OSD([sQuery(id+"F0.wireOp",EDGE,"E0"),sQuery(id+"F0.wireOp",EDGE,"E1"),sQuery(id+"F0.wireOp",EDGE,"E5.trimOffspring"),sQuery(id+"F0.wireOp",EDGE,"E6.trimOffspring"),sQuery(id+"F0.wireOp",EDGE,"E7"),sQuery(id+"F0.wireOp",EDGE,"E8.0"),sQuery(id+"F0.wireOp",EDGE,"E8.1"),sQuery(id+"F0.wireOp",EDGE,"E8.2"),sQuery(id+"F0.wireOp",EDGE,"E8.3"),sQuery(id+"F0.wireOp",EDGE,"E8.4"),sQuery(id+"F0.wireOp",EDGE,"E8.5"),sQuery(id+"F0.wireOp",EDGE,"E13.0"),sQuery(id+"F0.wireOp",EDGE,"E13.1"),sQuery(id+"F0.wireOp",EDGE,"E13.2"),sQuery(id+"F0.wireOp",EDGE,"E13.3"),sQuery(id+"F0.wireOp",EDGE,"E13.4"),sQuery(id+"F0.wireOp",EDGE,"E13.5"),sQuery(id+"F0.wireOp",EDGE,"E16.1.1"),subQ1,sQuery(id+"F0.wireOp",EDGE,"E16.1.5"),sQuery(id+"F0.wireOp",EDGE,"E16.1.8"),sQuery(id+"F0.wireOp",EDGE,"E16.1.9"),sQuery(id+"F0.wireOp",EDGE,"E16.1.10"),sQuery(id+"F0.wireOp",EDGE,"E16.1.12"),subQ0,sQuery(id+"F0.wireOp",EDGE,"E16.1.16"),sQuery(id+"F0.wireOp",EDGE,"E16.1.18"),sQuery(id+"F0.wireOp",EDGE,"E16.1.25"),sQuery(id+"F0.wireOp",EDGE,"E16.1.26"),sQuery(id+"F0.wireOp",EDGE,"E16.1.27"),sQuery(id+"F0.wireOp",EDGE,"E16.1.29"),sQuery(id+"F0.wireOp",EDGE,"E16.1.30"),sQuery(id+"F0.wireOp",EDGE,"E16.2.1"),sQuery(id+"F0.wireOp",EDGE,"E16.2.4"),sQuery(id+"F0.wireOp",EDGE,"E16.2.5"),sQuery(id+"F0.wireOp",EDGE,"E16.2.8"),sQuery(id+"F0.wireOp",EDGE,"E16.2.9"),sQuery(id+"F0.wireOp",EDGE,"E16.2.10"),sQuery(id+"F0.wireOp",EDGE,"E16.2.12"),sQuery(id+"F0.wireOp",EDGE,"E16.2.14"),sQuery(id+"F0.wireOp",EDGE,"E16.2.16"),sQuery(id+"F0.wireOp",EDGE,"E16.2.18"),sQuery(id+"F0.wireOp",EDGE,"E16.2.25"),sQuery(id+"F0.wireOp",EDGE,"E16.2.26"),sQuery(id+"F0.wireOp",EDGE,"E16.2.27"),sQuery(id+"F0.wireOp",EDGE,"E16.2.29"),sQuery(id+"F0.wireOp",EDGE,"E16.2.30")])],"isStart":true})],"blendedInto":[makeQuery(id+"F1.opExtrude","CAP_FACE",FACE,{"disambiguationData":[OSD([sQuery(id+"F0.wireOp",EDGE,"E0"),sQuery(id+"F0.wireOp",EDGE,"E1"),sQuery(id+"F0.wireOp",EDGE,"E5.trimOffspring"),sQuery(id+"F0.wireOp",EDGE,"E6.trimOffspring"),sQuery(id+"F0.wireOp",EDGE,"E7"),sQuery(id+"F0.wireOp",EDGE,"E8.0"),sQuery(id+"F0.wireOp",EDGE,"E8.1"),sQuery(id+"F0.wireOp",EDGE,"E8.2"),sQuery(id+"F0.wireOp",EDGE,"E8.3"),sQuery(id+"F0.wireOp",EDGE,"E8.4"),sQuery(id+"F0.wireOp",EDGE,"E8.5"),sQuery(id+"F0.wireOp",EDGE,"E13.0"),sQuery(id+"F0.wireOp",EDGE,"E13.1"),sQuery(id+"F0.wireOp",EDGE,"E13.2"),sQuery(id+"F0.wireOp",EDGE,"E13.3"),sQuery(id+"F0.wireOp",EDGE,"E13.4"),sQuery(id+"F0.wireOp",EDGE,"E13.5"),sQuery(id+"F0.wireOp",EDGE,"E16.1.1"),subQ1,sQuery(id+"F0.wireOp",EDGE,"E16.1.5"),sQuery(id+"F0.wireOp",EDGE,"E16.1.8"),sQuery(id+"F0.wireOp",EDGE,"E16.1.9"),sQuery(id+"F0.wireOp",EDGE,"E16.1.10"),sQuery(id+"F0.wireOp",EDGE,"E16.1.12"),subQ0,sQuery(id+"F0.wireOp",EDGE,"E16.1.16"),sQuery(id+"F0.wireOp",EDGE,"E16.1.18"),sQuery(id+"F0.wireOp",EDGE,"E16.1.25"),sQuery(id+"F0.wireOp",EDGE,"E16.1.26"),sQuery(id+"F0.wireOp",EDGE,"E16.1.27"),sQuery(id+"F0.wireOp",EDGE,"E16.1.29"),sQuery(id+"F0.wireOp",EDGE,"E16.1.30"),sQuery(id+"F0.wireOp",EDGE,"E16.2.1"),sQuery(id+"F0.wireOp",EDGE,"E16.2.4"),sQuery(id+"F0.wireOp",EDGE,"E16.2.5"),sQuery(id+"F0.wireOp",EDGE,"E16.2.8"),sQuery(id+"F0.wireOp",EDGE,"E16.2.9"),sQuery(id+"F0.wireOp",EDGE,"E16.2.10"),sQuery(id+"F0.wireOp",EDGE,"E16.2.12"),sQuery(id+"F0.wireOp",EDGE,"E16.2.14"),sQuery(id+"F0.wireOp",EDGE,"E16.2.16"),sQuery(id+"F0.wireOp",EDGE,"E16.2.18"),sQuery(id+"F0.wireOp",EDGE,"E16.2.25"),sQuery(id+"F0.wireOp",EDGE,"E16.2.26"),sQuery(id+"F0.wireOp",EDGE,"E16.2.27"),sQuery(id+"F0.wireOp",EDGE,"E16.2.29"),sQuery(id+"F0.wireOp",EDGE,"E16.2.30")])],"isStart":true})]});}
            var Q4;
            {var subQ0=sQuery(id+"F0.wireOp",EDGE,"E16.2.14");var subQ1=sQuery(id+"F0.wireOp",EDGE,"E16.2.4");Q4=makeQuery(id+"F2.opFillet","BLEND_EDGE",EDGE,{"blendedFrom":[makeQuery(id+"F1.opExtrude","SWEPT_EDGE",EDGE,{"disambiguationData":[OSD([subQ1,subQ0])]}),makeQuery(id+"F1.opExtrude","CAP_FACE",FACE,{"disambiguationData":[OSD([sQuery(id+"F0.wireOp",EDGE,"E0"),sQuery(id+"F0.wireOp",EDGE,"E1"),sQuery(id+"F0.wireOp",EDGE,"E5.trimOffspring"),sQuery(id+"F0.wireOp",EDGE,"E6.trimOffspring"),sQuery(id+"F0.wireOp",EDGE,"E7"),sQuery(id+"F0.wireOp",EDGE,"E8.0"),sQuery(id+"F0.wireOp",EDGE,"E8.1"),sQuery(id+"F0.wireOp",EDGE,"E8.2"),sQuery(id+"F0.wireOp",EDGE,"E8.3"),sQuery(id+"F0.wireOp",EDGE,"E8.4"),sQuery(id+"F0.wireOp",EDGE,"E8.5"),sQuery(id+"F0.wireOp",EDGE,"E13.0"),sQuery(id+"F0.wireOp",EDGE,"E13.1"),sQuery(id+"F0.wireOp",EDGE,"E13.2"),sQuery(id+"F0.wireOp",EDGE,"E13.3"),sQuery(id+"F0.wireOp",EDGE,"E13.4"),sQuery(id+"F0.wireOp",EDGE,"E13.5"),sQuery(id+"F0.wireOp",EDGE,"E16.1.1"),sQuery(id+"F0.wireOp",EDGE,"E16.1.4"),sQuery(id+"F0.wireOp",EDGE,"E16.1.5"),sQuery(id+"F0.wireOp",EDGE,"E16.1.8"),sQuery(id+"F0.wireOp",EDGE,"E16.1.9"),sQuery(id+"F0.wireOp",EDGE,"E16.1.10"),sQuery(id+"F0.wireOp",EDGE,"E16.1.12"),sQuery(id+"F0.wireOp",EDGE,"E16.1.14"),sQuery(id+"F0.wireOp",EDGE,"E16.1.16"),sQuery(id+"F0.wireOp",EDGE,"E16.1.18"),sQuery(id+"F0.wireOp",EDGE,"E16.1.25"),sQuery(id+"F0.wireOp",EDGE,"E16.1.26"),sQuery(id+"F0.wireOp",EDGE,"E16.1.27"),sQuery(id+"F0.wireOp",EDGE,"E16.1.29"),sQuery(id+"F0.wireOp",EDGE,"E16.1.30"),sQuery(id+"F0.wireOp",EDGE,"E16.2.1"),subQ1,sQuery(id+"F0.wireOp",EDGE,"E16.2.5"),sQuery(id+"F0.wireOp",EDGE,"E16.2.8"),sQuery(id+"F0.wireOp",EDGE,"E16.2.9"),sQuery(id+"F0.wireOp",EDGE,"E16.2.10"),sQuery(id+"F0.wireOp",EDGE,"E16.2.12"),subQ0,sQuery(id+"F0.wireOp",EDGE,"E16.2.16"),sQuery(id+"F0.wireOp",EDGE,"E16.2.18"),sQuery(id+"F0.wireOp",EDGE,"E16.2.25"),sQuery(id+"F0.wireOp",EDGE,"E16.2.26"),sQuery(id+"F0.wireOp",EDGE,"E16.2.27"),sQuery(id+"F0.wireOp",EDGE,"E16.2.29"),sQuery(id+"F0.wireOp",EDGE,"E16.2.30")])],"isStart":false})],"blendedInto":[makeQuery(id+"F1.opExtrude","CAP_FACE",FACE,{"disambiguationData":[OSD([sQuery(id+"F0.wireOp",EDGE,"E0"),sQuery(id+"F0.wireOp",EDGE,"E1"),sQuery(id+"F0.wireOp",EDGE,"E5.trimOffspring"),sQuery(id+"F0.wireOp",EDGE,"E6.trimOffspring"),sQuery(id+"F0.wireOp",EDGE,"E7"),sQuery(id+"F0.wireOp",EDGE,"E8.0"),sQuery(id+"F0.wireOp",EDGE,"E8.1"),sQuery(id+"F0.wireOp",EDGE,"E8.2"),sQuery(id+"F0.wireOp",EDGE,"E8.3"),sQuery(id+"F0.wireOp",EDGE,"E8.4"),sQuery(id+"F0.wireOp",EDGE,"E8.5"),sQuery(id+"F0.wireOp",EDGE,"E13.0"),sQuery(id+"F0.wireOp",EDGE,"E13.1"),sQuery(id+"F0.wireOp",EDGE,"E13.2"),sQuery(id+"F0.wireOp",EDGE,"E13.3"),sQuery(id+"F0.wireOp",EDGE,"E13.4"),sQuery(id+"F0.wireOp",EDGE,"E13.5"),sQuery(id+"F0.wireOp",EDGE,"E16.1.1"),sQuery(id+"F0.wireOp",EDGE,"E16.1.4"),sQuery(id+"F0.wireOp",EDGE,"E16.1.5"),sQuery(id+"F0.wireOp",EDGE,"E16.1.8"),sQuery(id+"F0.wireOp",EDGE,"E16.1.9"),sQuery(id+"F0.wireOp",EDGE,"E16.1.10"),sQuery(id+"F0.wireOp",EDGE,"E16.1.12"),sQuery(id+"F0.wireOp",EDGE,"E16.1.14"),sQuery(id+"F0.wireOp",EDGE,"E16.1.16"),sQuery(id+"F0.wireOp",EDGE,"E16.1.18"),sQuery(id+"F0.wireOp",EDGE,"E16.1.25"),sQuery(id+"F0.wireOp",EDGE,"E16.1.26"),sQuery(id+"F0.wireOp",EDGE,"E16.1.27"),sQuery(id+"F0.wireOp",EDGE,"E16.1.29"),sQuery(id+"F0.wireOp",EDGE,"E16.1.30"),sQuery(id+"F0.wireOp",EDGE,"E16.2.1"),subQ1,sQuery(id+"F0.wireOp",EDGE,"E16.2.5"),sQuery(id+"F0.wireOp",EDGE,"E16.2.8"),sQuery(id+"F0.wireOp",EDGE,"E16.2.9"),sQuery(id+"F0.wireOp",EDGE,"E16.2.10"),sQuery(id+"F0.wireOp",EDGE,"E16.2.12"),subQ0,sQuery(id+"F0.wireOp",EDGE,"E16.2.16"),sQuery(id+"F0.wireOp",EDGE,"E16.2.18"),sQuery(id+"F0.wireOp",EDGE,"E16.2.25"),sQuery(id+"F0.wireOp",EDGE,"E16.2.26"),sQuery(id+"F0.wireOp",EDGE,"E16.2.27"),sQuery(id+"F0.wireOp",EDGE,"E16.2.29"),sQuery(id+"F0.wireOp",EDGE,"E16.2.30")])],"isStart":false})]});}
            var Q5;
            {var subQ0=sQuery(id+"F0.wireOp",EDGE,"E16.2.14");var subQ1=sQuery(id+"F0.wireOp",EDGE,"E16.2.4");Q5=makeQuery(id+"F2.opFillet","BLEND_EDGE",EDGE,{"blendedFrom":[makeQuery(id+"F1.opExtrude","SWEPT_EDGE",EDGE,{"disambiguationData":[OSD([subQ1,subQ0])]}),makeQuery(id+"F1.opExtrude","CAP_FACE",FACE,{"disambiguationData":[OSD([sQuery(id+"F0.wireOp",EDGE,"E0"),sQuery(id+"F0.wireOp",EDGE,"E1"),sQuery(id+"F0.wireOp",EDGE,"E5.trimOffspring"),sQuery(id+"F0.wireOp",EDGE,"E6.trimOffspring"),sQuery(id+"F0.wireOp",EDGE,"E7"),sQuery(id+"F0.wireOp",EDGE,"E8.0"),sQuery(id+"F0.wireOp",EDGE,"E8.1"),sQuery(id+"F0.wireOp",EDGE,"E8.2"),sQuery(id+"F0.wireOp",EDGE,"E8.3"),sQuery(id+"F0.wireOp",EDGE,"E8.4"),sQuery(id+"F0.wireOp",EDGE,"E8.5"),sQuery(id+"F0.wireOp",EDGE,"E13.0"),sQuery(id+"F0.wireOp",EDGE,"E13.1"),sQuery(id+"F0.wireOp",EDGE,"E13.2"),sQuery(id+"F0.wireOp",EDGE,"E13.3"),sQuery(id+"F0.wireOp",EDGE,"E13.4"),sQuery(id+"F0.wireOp",EDGE,"E13.5"),sQuery(id+"F0.wireOp",EDGE,"E16.1.1"),sQuery(id+"F0.wireOp",EDGE,"E16.1.4"),sQuery(id+"F0.wireOp",EDGE,"E16.1.5"),sQuery(id+"F0.wireOp",EDGE,"E16.1.8"),sQuery(id+"F0.wireOp",EDGE,"E16.1.9"),sQuery(id+"F0.wireOp",EDGE,"E16.1.10"),sQuery(id+"F0.wireOp",EDGE,"E16.1.12"),sQuery(id+"F0.wireOp",EDGE,"E16.1.14"),sQuery(id+"F0.wireOp",EDGE,"E16.1.16"),sQuery(id+"F0.wireOp",EDGE,"E16.1.18"),sQuery(id+"F0.wireOp",EDGE,"E16.1.25"),sQuery(id+"F0.wireOp",EDGE,"E16.1.26"),sQuery(id+"F0.wireOp",EDGE,"E16.1.27"),sQuery(id+"F0.wireOp",EDGE,"E16.1.29"),sQuery(id+"F0.wireOp",EDGE,"E16.1.30"),sQuery(id+"F0.wireOp",EDGE,"E16.2.1"),subQ1,sQuery(id+"F0.wireOp",EDGE,"E16.2.5"),sQuery(id+"F0.wireOp",EDGE,"E16.2.8"),sQuery(id+"F0.wireOp",EDGE,"E16.2.9"),sQuery(id+"F0.wireOp",EDGE,"E16.2.10"),sQuery(id+"F0.wireOp",EDGE,"E16.2.12"),subQ0,sQuery(id+"F0.wireOp",EDGE,"E16.2.16"),sQuery(id+"F0.wireOp",EDGE,"E16.2.18"),sQuery(id+"F0.wireOp",EDGE,"E16.2.25"),sQuery(id+"F0.wireOp",EDGE,"E16.2.26"),sQuery(id+"F0.wireOp",EDGE,"E16.2.27"),sQuery(id+"F0.wireOp",EDGE,"E16.2.29"),sQuery(id+"F0.wireOp",EDGE,"E16.2.30")])],"isStart":true})],"blendedInto":[makeQuery(id+"F1.opExtrude","CAP_FACE",FACE,{"disambiguationData":[OSD([sQuery(id+"F0.wireOp",EDGE,"E0"),sQuery(id+"F0.wireOp",EDGE,"E1"),sQuery(id+"F0.wireOp",EDGE,"E5.trimOffspring"),sQuery(id+"F0.wireOp",EDGE,"E6.trimOffspring"),sQuery(id+"F0.wireOp",EDGE,"E7"),sQuery(id+"F0.wireOp",EDGE,"E8.0"),sQuery(id+"F0.wireOp",EDGE,"E8.1"),sQuery(id+"F0.wireOp",EDGE,"E8.2"),sQuery(id+"F0.wireOp",EDGE,"E8.3"),sQuery(id+"F0.wireOp",EDGE,"E8.4"),sQuery(id+"F0.wireOp",EDGE,"E8.5"),sQuery(id+"F0.wireOp",EDGE,"E13.0"),sQuery(id+"F0.wireOp",EDGE,"E13.1"),sQuery(id+"F0.wireOp",EDGE,"E13.2"),sQuery(id+"F0.wireOp",EDGE,"E13.3"),sQuery(id+"F0.wireOp",EDGE,"E13.4"),sQuery(id+"F0.wireOp",EDGE,"E13.5"),sQuery(id+"F0.wireOp",EDGE,"E16.1.1"),sQuery(id+"F0.wireOp",EDGE,"E16.1.4"),sQuery(id+"F0.wireOp",EDGE,"E16.1.5"),sQuery(id+"F0.wireOp",EDGE,"E16.1.8"),sQuery(id+"F0.wireOp",EDGE,"E16.1.9"),sQuery(id+"F0.wireOp",EDGE,"E16.1.10"),sQuery(id+"F0.wireOp",EDGE,"E16.1.12"),sQuery(id+"F0.wireOp",EDGE,"E16.1.14"),sQuery(id+"F0.wireOp",EDGE,"E16.1.16"),sQuery(id+"F0.wireOp",EDGE,"E16.1.18"),sQuery(id+"F0.wireOp",EDGE,"E16.1.25"),sQuery(id+"F0.wireOp",EDGE,"E16.1.26"),sQuery(id+"F0.wireOp",EDGE,"E16.1.27"),sQuery(id+"F0.wireOp",EDGE,"E16.1.29"),sQuery(id+"F0.wireOp",EDGE,"E16.1.30"),sQuery(id+"F0.wireOp",EDGE,"E16.2.1"),subQ1,sQuery(id+"F0.wireOp",EDGE,"E16.2.5"),sQuery(id+"F0.wireOp",EDGE,"E16.2.8"),sQuery(id+"F0.wireOp",EDGE,"E16.2.9"),sQuery(id+"F0.wireOp",EDGE,"E16.2.10"),sQuery(id+"F0.wireOp",EDGE,"E16.2.12"),subQ0,sQuery(id+"F0.wireOp",EDGE,"E16.2.16"),sQuery(id+"F0.wireOp",EDGE,"E16.2.18"),sQuery(id+"F0.wireOp",EDGE,"E16.2.25"),sQuery(id+"F0.wireOp",EDGE,"E16.2.26"),sQuery(id+"F0.wireOp",EDGE,"E16.2.27"),sQuery(id+"F0.wireOp",EDGE,"E16.2.29"),sQuery(id+"F0.wireOp",EDGE,"E16.2.30")])],"isStart":true})]});}
            fillet(context, id + "F5", {"entities" : qUnion([Q0, Q1, Q2, Q3, Q4, Q5]), "radius" : 1.6 * mm, "tangentPropagation" : true, "allowEdgeOverflow" : false});
        }
    });
